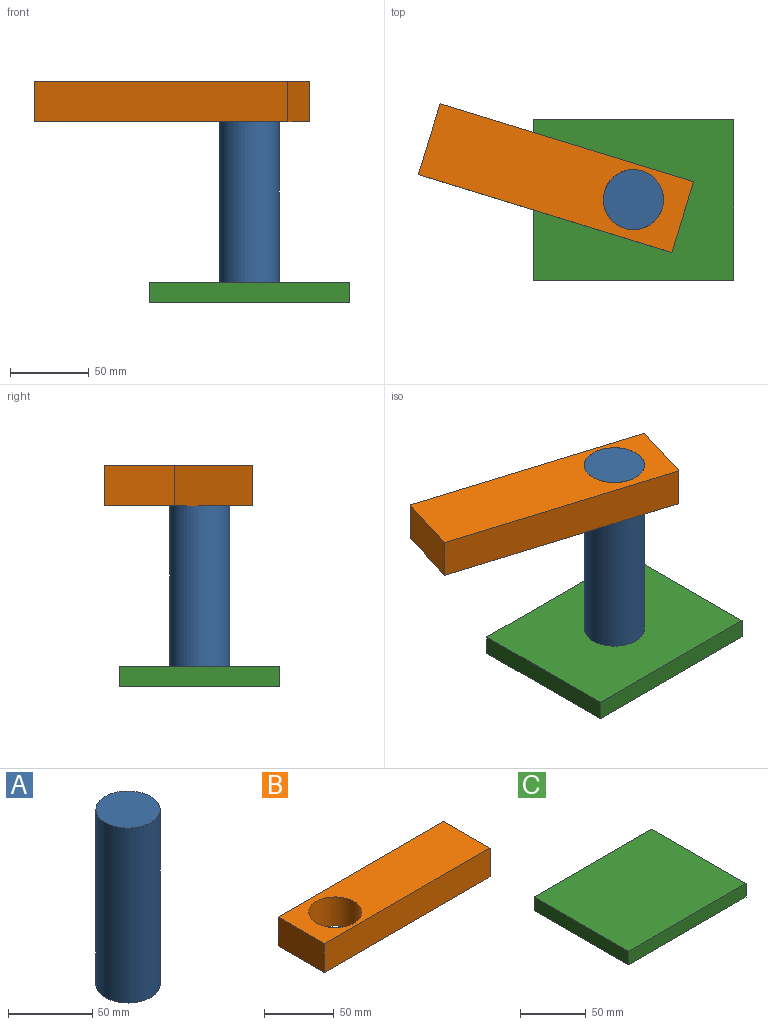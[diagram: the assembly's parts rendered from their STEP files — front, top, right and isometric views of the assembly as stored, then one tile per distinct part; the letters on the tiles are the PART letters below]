
ASSEMBLY  parts=3 mates=2
PART A: 3 faces, bbox 38.1x38.1x127 mm
  f0: cylinder r=19.05mm len=127mm, axis (0,0,-1), area 15201.2mm2, adj f1,f2
  f1: plane 38.1x38.1mm, normal (0,0,1), area 1140.1mm2, adj f0
  f2: plane 38.1x38.1mm, normal (0,0,-1), area 1140.1mm2, adj f0
PART B: 7 faces, bbox 168x46.9x25.4 mm
  f0: plane 168.03x25.4mm, normal (0,1,0), area 4268mm2, adj f1,f4,f5,f6
  f1: plane 46.89x25.4mm, normal (-1,0,0), area 1191.1mm2, adj f0,f2,f5,f6
  f2: plane 168.03x25.4mm, normal (0,-1,0), area 4268mm2, adj f1,f4,f5,f6
  f3: cylinder r=19.05mm len=38.1mm, axis (0,0,-1), area 3040.2mm2, adj f5,f6
  f4: plane 46.89x25.4mm, normal (1,0,0), area 1191.1mm2, adj f0,f2,f5,f6
  f5: plane 168.03x46.89mm, normal (0,0,1), area 6739.3mm2, adj f0,f1,f2,f3,f4
  f6: plane 168.03x46.89mm, normal (0,0,-1), area 6739.3mm2, adj f0,f1,f2,f3,f4
PART C: 6 faces, bbox 127x101.6x12.7 mm
  f0: plane 127x12.7mm, normal (0,-1,0), area 1612.9mm2, adj f1,f3,f4,f5
  f1: plane 101.6x12.7mm, normal (1,0,0), area 1290.3mm2, adj f0,f2,f4,f5
  f2: plane 127x12.7mm, normal (0,1,0), area 1612.9mm2, adj f1,f3,f4,f5
  f3: plane 101.6x12.7mm, normal (-1,0,0), area 1290.3mm2, adj f0,f2,f4,f5
  f4: plane 127x101.6mm, normal (0,0,1), area 12903.2mm2, adj f0,f1,f2,f3
  f5: plane 127x101.6mm, normal (0,0,-1), area 12903.2mm2, adj f0,f1,f2,f3
PLACE A t=(0.05,-3.77,0.66)mm
PLACE B rot(axis=(0,0,1),162.9deg) t=(0.05,-3.77,-24.74)mm
PLACE C t=(0.05,-3.77,-12.04)mm fixed
MATE revolute B.f3 <-> A.f0  axis (0,0,-1) through (0.05,-3.77,127.66)mm
MATE fastened C.f4 <-> A.f0  axis (0,0,1) through (0.05,-3.77,0.66)mm
